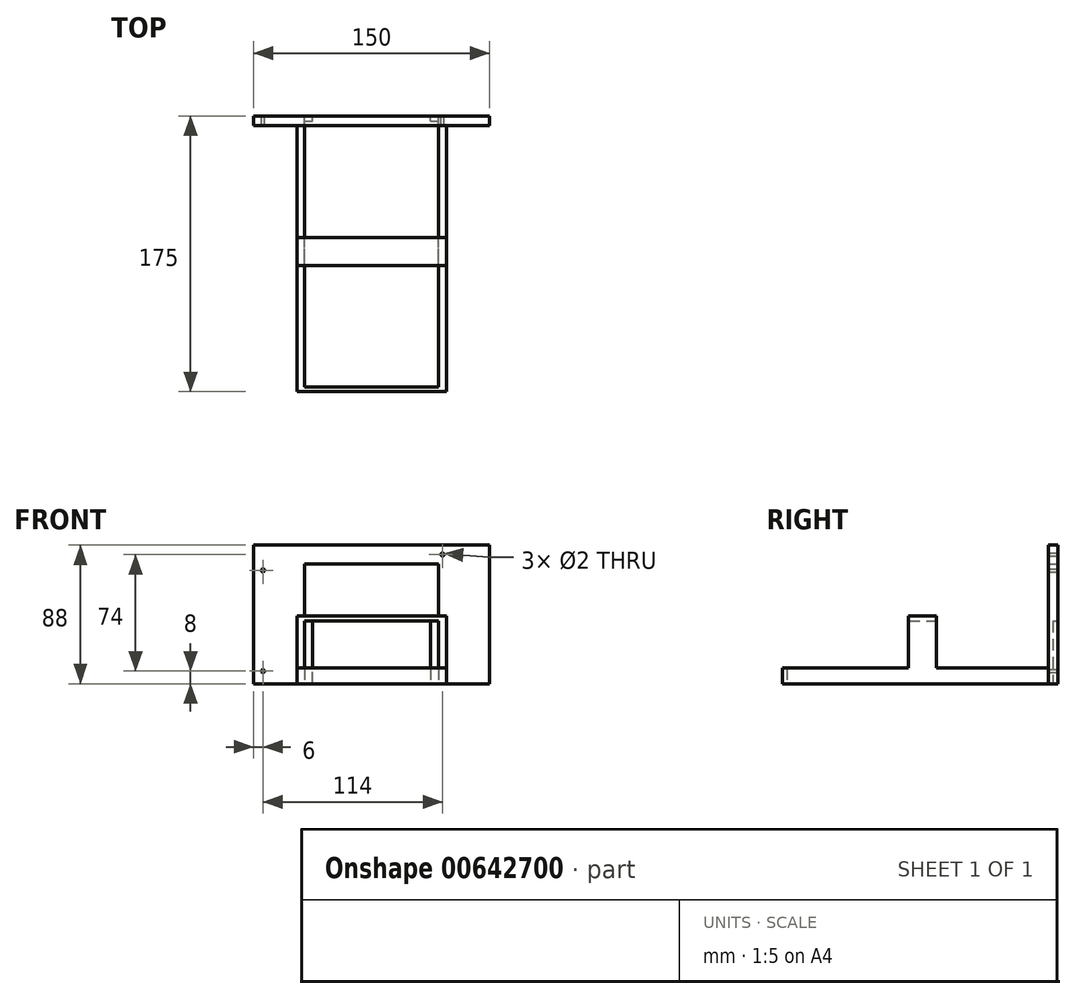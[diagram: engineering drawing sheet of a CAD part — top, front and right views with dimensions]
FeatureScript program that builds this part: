
annotation { "Feature Type Name" : "Feature", "Feature Type Description" : "" }
export const myFeature = defineFeature(function(context is Context, id is Id, definition is map)
    precondition{}
    {
        {
            var Q0;
            Q0=qCreatedBy(makeId("Front.planeOp"),FACE);
            var sketch = newSketch(context, id + "F0", { "sketchPlane" : qUnion([Q0])});
            skLineSegment(sketch, "E0", {"start": v(-75, 48) * mm, "end": v(75, 48) * mm});
            skPoint(sketch, "E1", {"position": v(-69, 32) * mm});
            skPoint(sketch, "E2", {"position": v(45, 42) * mm});
            skPoint(sketch, "E3", {"position": v(-69, -32) * mm});
            skLineSegment(sketch, "E4", {"start": v(-75, 48) * mm, "end": v(-75, -40) * mm});
            skLineSegment(sketch, "E5", {"start": v(42.5, -30) * mm, "end": v(47.5, -30) * mm});
            skLineSegment(sketch, "E6", {"start": v(42.5, -30) * mm, "end": v(42.5, -40) * mm});
            skLineSegment(sketch, "E7", {"start": v(47.5, -30) * mm, "end": v(47.5, -40) * mm});
            skLineSegment(sketch, "E8", {"start": v(0, 0) * mm, "end": v(0, -40) * mm, "construction": true});
            skLineSegment(sketch, "E9", {"start": v(42.5, -30) * mm, "end": v(42.5, 36) * mm});
            skLineSegment(sketch, "E10", {"start": v(-42.5, 36) * mm, "end": v(75, 36) * mm});
            skLineSegment(sketch, "E11", {"start": v(-42.5, 36) * mm, "end": v(-42.5, -40) * mm});
            skLineSegment(sketch, "E12", {"start": v(-47.5, 3) * mm, "end": v(47.5, 3) * mm});
            skLineSegment(sketch, "E13", {"start": v(47.5, 3) * mm, "end": v(47.5, -30) * mm});
            skLineSegment(sketch, "E14", {"start": v(47.5, 0) * mm, "end": v(-47.5, 0) * mm});
            skLineSegment(sketch, "E15", {"start": v(-37.5, -40) * mm, "end": v(-37.5, 0) * mm});
            skLineSegment(sketch, "E16", {"start": v(37.5, 0) * mm, "end": v(37.5, -40) * mm});
            skLineSegment(sketch, "E17", {"start": v(-47.5, 3) * mm, "end": v(-47.5, -40) * mm});
            skLineSegment(sketch, "E18", {"start": v(-75, -40) * mm, "end": v(75, -40) * mm});
            skLineSegment(sketch, "E19", {"start": v(-47.5, -30) * mm, "end": v(-42.5, -30) * mm});
            skLineSegment(sketch, "E20", {"start": v(75, 48) * mm, "end": v(75, -40) * mm});
            skLineSegment(sketch, "E21", {"start": v(42.5, -30) * mm, "end": v(37.5, -30) * mm});
            skLineSegment(sketch, "E22", {"start": v(-42.5, -30) * mm, "end": v(-37.5, -30) * mm});
            skLineSegment(sketch, "E23", {"start": v(37.5, -30) * mm, "end": v(-37.5, -30) * mm});
            skSolve(sketch);
        }
        {
            var Q0;
            Q0=makeQuery(id+"F0.imprint","IMPRINT",FACE,{"disambiguationData":[TD([[makeQuery(id+"F0.imprint","IMPRINT",EDGE,{"derivedFrom":sQuery(id+"F0.wireOp",EDGE,"E0")}),-1.0]])]});
            var Q1;
            {var subQ6=sQuery(id+"F0.wireOp",EDGE,"E7");Q1=makeQuery(id+"F0.imprint","IMPRINT",FACE,{"disambiguationData":[TD([[makeQuery(id+"F0.imprint","IMPRINT",EDGE,{"derivedFrom":subQ6}),1.0]])]});}
            var Q2;
            {var subQ0=sQuery(id+"F0.wireOp",EDGE,"E14");var subQ1=sQuery(id+"F0.wireOp",EDGE,"E9");var subQ2=makeQuery(id+"F0.imprint","INTERSECT",VERTEX,{"derivedFrom":[subQ1,subQ0]});Q2=makeQuery(id+"F0.imprint","IMPRINT",FACE,{"disambiguationData":[TD([[makeQuery(id+"F0.imprint","IMPRINT",EDGE,{"disambiguationData":[TD([[subQ2,-1.0]])],"derivedFrom":subQ1}),-1.0]])]});}
            var Q3;
            {var subQ0=sQuery(id+"F0.wireOp",EDGE,"E5");Q3=makeQuery(id+"F0.imprint","IMPRINT",FACE,{"disambiguationData":[TD([[makeQuery(id+"F0.imprint","IMPRINT",EDGE,{"derivedFrom":subQ0}),1.0]])]});}
            var Q4;
            Q4=makeQuery(id+"F0.imprint","IMPRINT",FACE,{"disambiguationData":[TD([[makeQuery(id+"F0.imprint","IMPRINT",EDGE,{"derivedFrom":sQuery(id+"F0.wireOp",EDGE,"4DkXp1rW-LEH0-5AJK-n7uf-6DjnthERH1ku")}),1.0]])]});
            var Q5;
            {var subQ0=sQuery(id+"F0.wireOp",EDGE,"E12");var subQ1=sQuery(id+"F0.wireOp",EDGE,"E11");var subQ2=makeQuery(id+"F0.imprint","INTERSECT",VERTEX,{"derivedFrom":[subQ1,subQ0]});Q5=makeQuery(id+"F0.imprint","IMPRINT",FACE,{"disambiguationData":[TD([[makeQuery(id+"F0.imprint","IMPRINT",EDGE,{"disambiguationData":[TD([[subQ2,-1.0]])],"derivedFrom":subQ1}),-1.0]])]});}
            var Q6;
            {var subQ0=sQuery(id+"F0.wireOp",EDGE,"E14");var subQ1=sQuery(id+"F0.wireOp",EDGE,"E11");var subQ2=makeQuery(id+"F0.imprint","INTERSECT",VERTEX,{"derivedFrom":[subQ1,subQ0]});Q6=makeQuery(id+"F0.imprint","IMPRINT",FACE,{"disambiguationData":[TD([[makeQuery(id+"F0.imprint","IMPRINT",EDGE,{"disambiguationData":[TD([[subQ2,-1.0]])],"derivedFrom":subQ1}),-1.0]])]});}
            var Q7;
            {var subQ0=sQuery(id+"F0.wireOp",EDGE,"awgAnmQw-xq4Q-FcJA-eC86-ohq8b9gSleHf");Q7=makeQuery(id+"F0.imprint","IMPRINT",FACE,{"disambiguationData":[TD([[makeQuery(id+"F0.imprint","IMPRINT",EDGE,{"derivedFrom":subQ0}),1.0]])]});}
            extrude(context, id + "F1", {"entities" : qUnion([Q0, Q1, Q2, Q3, Q4, Q5, Q6, Q7]), "depth" : 6 * mm, "offsetDistance" : 25 * mm});
        }
        {
            var Q0;
            {var subQ3=sQuery(id+"F0.wireOp",EDGE,"E19");Q0=makeQuery(id+"F0.imprint","IMPRINT",FACE,{"disambiguationData":[TD([[makeQuery(id+"F0.imprint","IMPRINT",EDGE,{"derivedFrom":subQ3}),-1.0]])]});}
            var Q1;
            Q1=makeQuery(id+"F0.imprint","IMPRINT",FACE,{"disambiguationData":[TD([[makeQuery(id+"F0.imprint","IMPRINT",EDGE,{"derivedFrom":sQuery(id+"F0.wireOp",EDGE,"E5")}),-1.0]])]});
            extrude(context, id + "F2", {"entities" : qUnion([Q0, Q1]), "operationType" : NewBodyOperationType.ADD, "depth" : 175 * mm, "offsetDistance" : 25 * mm});
        }
        {
            var Q0;
            {var subQ0=sQuery(id+"F0.wireOp",EDGE,"E22");Q0=makeQuery(id+"F0.imprint","IMPRINT",FACE,{"disambiguationData":[TD([[makeQuery(id+"F0.imprint","IMPRINT",EDGE,{"derivedFrom":subQ0}),1.0]])]});}
            var Q1;
            {var subQ3=sQuery(id+"F0.wireOp",EDGE,"E22");Q1=makeQuery(id+"F0.imprint","IMPRINT",FACE,{"disambiguationData":[TD([[makeQuery(id+"F0.imprint","IMPRINT",EDGE,{"derivedFrom":subQ3}),-1.0]])]});}
            var Q2;
            {var subQ0=sQuery(id+"F0.wireOp",EDGE,"E6");Q2=makeQuery(id+"F0.imprint","IMPRINT",FACE,{"disambiguationData":[TD([[makeQuery(id+"F0.imprint","IMPRINT",EDGE,{"derivedFrom":subQ0}),-1.0]])]});}
            var Q3;
            {var subQ0=sQuery(id+"F0.wireOp",EDGE,"E21");Q3=makeQuery(id+"F0.imprint","IMPRINT",FACE,{"disambiguationData":[TD([[makeQuery(id+"F0.imprint","IMPRINT",EDGE,{"derivedFrom":subQ0}),-1.0]])]});}
            extrude(context, id + "F3", {"entities" : qUnion([Q0, Q1, Q2, Q3]), "operationType" : NewBodyOperationType.ADD, "depth" : 3 * mm, "offsetDistance" : 25 * mm});
        }
        {
            var Q0;
            {var subQ3=sQuery(id+"F0.wireOp",EDGE,"E22");Q0=makeQuery(id+"F0.imprint","IMPRINT",FACE,{"disambiguationData":[TD([[makeQuery(id+"F0.imprint","IMPRINT",EDGE,{"derivedFrom":subQ3}),-1.0]])]});}
            var Q1;
            {var subQ0=sQuery(id+"F0.wireOp",EDGE,"E6");Q1=makeQuery(id+"F0.imprint","IMPRINT",FACE,{"disambiguationData":[TD([[makeQuery(id+"F0.imprint","IMPRINT",EDGE,{"derivedFrom":subQ0}),-1.0]])]});}
            var Q2;
            {var subQ3=sQuery(id+"F0.wireOp",EDGE,"E23");Q2=makeQuery(id+"F0.imprint","IMPRINT",FACE,{"disambiguationData":[TD([[makeQuery(id+"F0.imprint","IMPRINT",EDGE,{"derivedFrom":subQ3}),1.0]])]});}
            extrude(context, id + "F4", {"entities" : qUnion([Q0, Q1, Q2]), "operationType" : NewBodyOperationType.ADD, "depth" : 175 * mm, "offsetDistance" : 25 * mm, "hasSecondDirection" : true, "secondDirectionOppositeDirection" : false, "secondDirectionDepth" : 172 * mm});
        }
        {
            var Q0;
            {var subQ0=sQuery(id+"F0.wireOp",EDGE,"E14");var subQ1=sQuery(id+"F0.wireOp",EDGE,"E11");var subQ2=makeQuery(id+"F0.imprint","INTERSECT",VERTEX,{"derivedFrom":[subQ1,subQ0]});Q0=makeQuery(id+"F0.imprint","IMPRINT",FACE,{"disambiguationData":[TD([[makeQuery(id+"F0.imprint","IMPRINT",EDGE,{"disambiguationData":[TD([[subQ2,-1.0]])],"derivedFrom":subQ1}),-1.0]])]});}
            var Q1;
            {var subQ0=sQuery(id+"F0.wireOp",EDGE,"awgAnmQw-xq4Q-FcJA-eC86-ohq8b9gSleHf");Q1=makeQuery(id+"F0.imprint","IMPRINT",FACE,{"disambiguationData":[TD([[makeQuery(id+"F0.imprint","IMPRINT",EDGE,{"derivedFrom":subQ0}),1.0]])]});}
            var Q2;
            Q2=makeQuery(id+"F0.imprint","IMPRINT",FACE,{"disambiguationData":[TD([[makeQuery(id+"F0.imprint","IMPRINT",EDGE,{"derivedFrom":sQuery(id+"F0.wireOp",EDGE,"4DkXp1rW-LEH0-5AJK-n7uf-6DjnthERH1ku")}),1.0]])]});
            var Q3;
            {var subQ0=sQuery(id+"F0.wireOp",EDGE,"E5");Q3=makeQuery(id+"F0.imprint","IMPRINT",FACE,{"disambiguationData":[TD([[makeQuery(id+"F0.imprint","IMPRINT",EDGE,{"derivedFrom":subQ0}),1.0]])]});}
            var Q4;
            {var subQ0=sQuery(id+"F0.wireOp",EDGE,"E14");var subQ1=sQuery(id+"F0.wireOp",EDGE,"E9");var subQ2=makeQuery(id+"F0.imprint","INTERSECT",VERTEX,{"derivedFrom":[subQ1,subQ0]});Q4=makeQuery(id+"F0.imprint","IMPRINT",FACE,{"disambiguationData":[TD([[makeQuery(id+"F0.imprint","IMPRINT",EDGE,{"disambiguationData":[TD([[subQ2,-1.0]])],"derivedFrom":subQ1}),1.0]])]});}
            var Q5;
            {var subQ0=sQuery(id+"F0.wireOp",EDGE,"E14");var subQ1=sQuery(id+"F0.wireOp",EDGE,"E9");var subQ2=makeQuery(id+"F0.imprint","INTERSECT",VERTEX,{"derivedFrom":[subQ1,subQ0]});Q5=makeQuery(id+"F0.imprint","IMPRINT",FACE,{"disambiguationData":[TD([[makeQuery(id+"F0.imprint","IMPRINT",EDGE,{"disambiguationData":[TD([[subQ2,-1.0]])],"derivedFrom":subQ1}),-1.0]])]});}
            var Q6;
            {var subQ0=sQuery(id+"F0.wireOp",EDGE,"E12");var subQ1=sQuery(id+"F0.wireOp",EDGE,"E11");var subQ2=makeQuery(id+"F0.imprint","INTERSECT",VERTEX,{"derivedFrom":[subQ1,subQ0]});Q6=makeQuery(id+"F0.imprint","IMPRINT",FACE,{"disambiguationData":[TD([[makeQuery(id+"F0.imprint","IMPRINT",EDGE,{"disambiguationData":[TD([[subQ2,-1.0]])],"derivedFrom":subQ1}),-1.0]])]});}
            extrude(context, id + "F5", {"entities" : qUnion([Q0, Q1, Q2, Q3, Q4, Q5, Q6]), "operationType" : NewBodyOperationType.ADD, "depth" : 95 * mm, "offsetDistance" : 25 * mm, "hasSecondDirection" : true, "secondDirectionOppositeDirection" : false, "secondDirectionDepth" : 77 * mm});
        }
        {
            var Q0;
            Q0=sQuery(id+"F0.wireOp",VERTEX,"E2");
            var Q1;
            Q1=sQuery(id+"F0.wireOp",VERTEX,"E1");
            var Q2;
            Q2=sQuery(id+"F0.wireOp",VERTEX,"E3");
            var Q3;
            Q3=makeQuery(id+"F1.opExtrude","SWEPT_BODY",BODY,{"disambiguationData":[OSD([sQuery(id+"F0.wireOp",EDGE,"E0"),sQuery(id+"F0.wireOp",EDGE,"E4"),sQuery(id+"F0.wireOp",EDGE,"pcj6ytS3-MFlx-J5F2-PC05-5FweqdKUbAkK"),sQuery(id+"F0.wireOp",EDGE,"0N0cjOJn-Wd7G-kqCc-ne4R-cvzpKWdOmqdB"),sQuery(id+"F0.wireOp",EDGE,"E5"),sQuery(id+"F0.wireOp",EDGE,"mlrlknkD-bBe7-3rBR-P4WU-71saSz7KTE6Z"),sQuery(id+"F0.wireOp",EDGE,"E7"),sQuery(id+"F0.wireOp",EDGE,"E9"),sQuery(id+"F0.wireOp",EDGE,"4ZPbSSiR-hYJ6-5o5G-SDtA-yqmf7H07boO1"),sQuery(id+"F0.wireOp",EDGE,"LmsuypSj-4mda-1Wmc-DN4n-yTUWO0szXO4v"),sQuery(id+"F0.wireOp",EDGE,"KYhPzbXK-b6JN-BFfd-Tdqo-g5fE9eHhGVG6"),sQuery(id+"F0.wireOp",EDGE,"E10"),sQuery(id+"F0.wireOp",EDGE,"E11"),sQuery(id+"F0.wireOp",EDGE,"NR4WwmMM-cyaB-Eq4f-n7Sb-6RSIFTwUsXkH")])]});
            hole(context, id + "F6", {"style" : HoleStyle.SIMPLE, "endStyle" : HoleEndStyle.THROUGH, "oppositeDirection" : true, "holeDiameter" : 2 * mm, "majorDiameter" : 5 * mm, "isTappedThrough" : true, "tappedDepth" : 12 * mm, "tapClearance" : 3, "locations" : qUnion([Q0, Q1, Q2]), "scope" : qUnion([Q3])});
        }
    });
